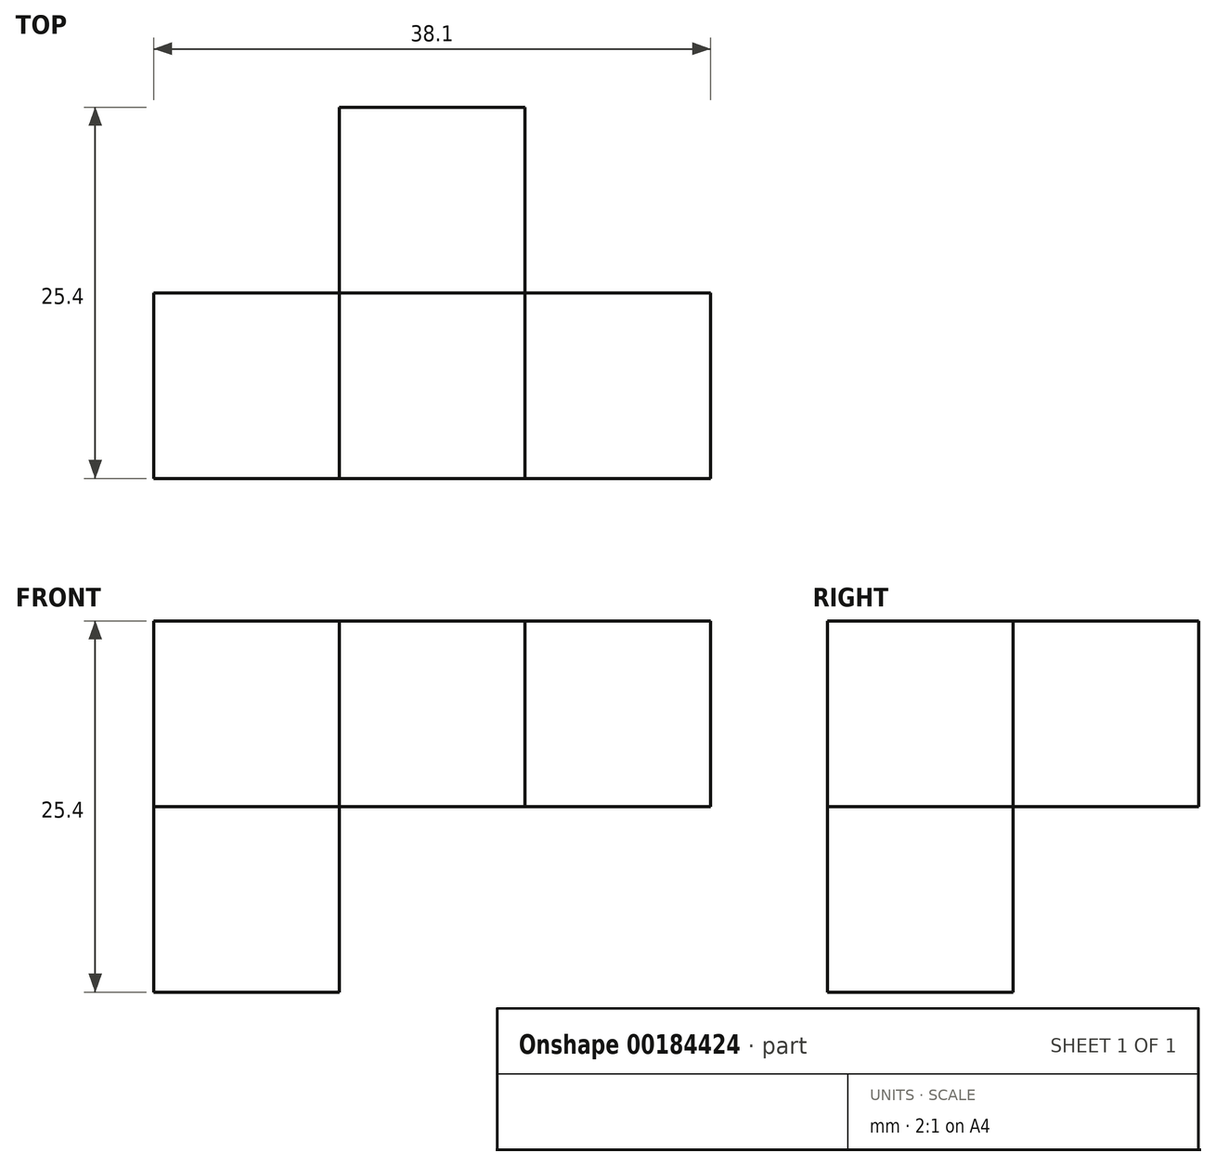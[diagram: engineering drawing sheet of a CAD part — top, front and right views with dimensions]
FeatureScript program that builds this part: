
annotation { "Feature Type Name" : "Feature", "Feature Type Description" : "" }
export const myFeature = defineFeature(function(context is Context, id is Id, definition is map)
    precondition{}
    {
        {
            var Q0;
            Q0=qCreatedBy(makeId("Front.planeOp"),FACE);
            var sketch = newSketch(context, id + "F0", { "sketchPlane" : qUnion([Q0])});
            skLineSegment(sketch, "E0.bottom", {"start": v(53.53, 16.57) * mm, "end": v(66.23, 16.57) * mm});
            skLineSegment(sketch, "E0.top", {"start": v(53.53, 3.87) * mm, "end": v(66.23, 3.87) * mm});
            skLineSegment(sketch, "E0.left", {"start": v(53.53, 16.57) * mm, "end": v(53.53, 3.87) * mm});
            skLineSegment(sketch, "E0.right", {"start": v(66.23, 16.57) * mm, "end": v(66.23, 3.87) * mm});
            skSolve(sketch);
        }
        {
            var Q0;
            Q0 = qSketchRegion(id + "F0", true);
            extrude(context, id + "F1", {"entities" : qUnion([Q0]), "depth" : 12.7 * mm});
        }
        {
            var Q0;
            Q0=makeQuery(id+"F1.opExtrude","SWEPT_EDGE",EDGE,{"disambiguationData":[OSD([sQuery(id+"F0.wireOp",EDGE,"E0.bottom"),sQuery(id+"F0.wireOp",EDGE,"E0.right")])]});
            cPoint(context, id + "F2", {"entities" : qUnion([Q0]), "parameter" : 0.5});
        }
        {
            var Q0;
            Q0=makeQuery(id+"F1.opExtrude","SWEPT_EDGE",EDGE,{"disambiguationData":[OSD([sQuery(id+"F0.wireOp",EDGE,"E0.bottom"),sQuery(id+"F0.wireOp",EDGE,"E0.left")])]});
            cPoint(context, id + "F3", {"entities" : qUnion([Q0]), "parameter" : 0.5});
        }
        {
            var Q0;
            Q0=makeQuery(id+"F1.opExtrude","SWEPT_BODY",BODY,{"disambiguationData":[OSD([sQuery(id+"F0.wireOp",EDGE,"E0.bottom"),sQuery(id+"F0.wireOp",EDGE,"E0.top"),sQuery(id+"F0.wireOp",EDGE,"E0.left"),sQuery(id+"F0.wireOp",EDGE,"E0.right")])]});
            var Q1;
            Q1 = qCreatedBy(id + "F2" ,VERTEX);
            var Q2;
            Q2 = qCreatedBy(id + "F3" ,VERTEX);
            transform(context, id + "F4", {"entities" : qUnion([Q0]), "transformType" : TransformType.TRANSLATION_ENTITY, "oppositeDirectionEntity" : false, "transformLine" : qUnion([Q1, Q2]), "makeCopy" : true});
        }
        {
            var Q0;
            Q0=makeQuery(id+"F4.opPattern","COPY",BODY,{"derivedFrom":makeQuery(id+"F1.opExtrude","SWEPT_BODY",BODY,{"disambiguationData":[OSD([sQuery(id+"F0.wireOp",EDGE,"E0.bottom"),sQuery(id+"F0.wireOp",EDGE,"E0.top"),sQuery(id+"F0.wireOp",EDGE,"E0.left"),sQuery(id+"F0.wireOp",EDGE,"E0.right")])]}),"instanceName":"1"});
            var Q1;
            Q1=makeQuery(id+"F4.opPattern","COPY",VERTEX,{"derivedFrom":makeQuery(id+"F1.opExtrude","CAP_VERTEX",VERTEX,{"disambiguationData":[OSD([sQuery(id+"F0.wireOp",EDGE,"E0.bottom"),sQuery(id+"F0.wireOp",EDGE,"E0.left")])],"isStart":false}),"instanceName":"1"});
            var Q2;
            Q2=makeQuery(id+"F4.opPattern","COPY",VERTEX,{"derivedFrom":makeQuery(id+"F1.opExtrude","CAP_VERTEX",VERTEX,{"disambiguationData":[OSD([sQuery(id+"F0.wireOp",EDGE,"E0.bottom"),sQuery(id+"F0.wireOp",EDGE,"E0.left")])],"isStart":true}),"instanceName":"1"});
            transform(context, id + "F5", {"entities" : qUnion([Q0]), "transformType" : TransformType.TRANSLATION_ENTITY, "oppositeDirectionEntity" : false, "transformLine" : qUnion([Q1, Q2]), "makeCopy" : true});
        }
        {
            var Q0;
            Q0=makeQuery(id+"F1.opExtrude","SWEPT_EDGE",EDGE,{"disambiguationData":[OSD([sQuery(id+"F0.wireOp",EDGE,"E0.bottom"),sQuery(id+"F0.wireOp",EDGE,"E0.left")])]});
            cPoint(context, id + "F6", {"entities" : qUnion([Q0]), "parameter" : 0.5});
        }
        {
            var Q0;
            Q0=makeQuery(id+"F4.opPattern","COPY",EDGE,{"derivedFrom":makeQuery(id+"F1.opExtrude","SWEPT_EDGE",EDGE,{"disambiguationData":[OSD([sQuery(id+"F0.wireOp",EDGE,"E0.bottom"),sQuery(id+"F0.wireOp",EDGE,"E0.left")])]}),"instanceName":"1"});
            cPoint(context, id + "F7", {"entities" : qUnion([Q0]), "parameter" : 0.5});
        }
        {
            var Q0;
            Q0=makeQuery(id+"F4.opPattern","COPY",BODY,{"derivedFrom":makeQuery(id+"F1.opExtrude","SWEPT_BODY",BODY,{"disambiguationData":[OSD([sQuery(id+"F0.wireOp",EDGE,"E0.bottom"),sQuery(id+"F0.wireOp",EDGE,"E0.top"),sQuery(id+"F0.wireOp",EDGE,"E0.left"),sQuery(id+"F0.wireOp",EDGE,"E0.right")])]}),"instanceName":"1"});
            var Q1;
            Q1 = qCreatedBy(id + "F6" ,VERTEX);
            var Q2;
            Q2 = qCreatedBy(id + "F7" ,VERTEX);
            transform(context, id + "F8", {"entities" : qUnion([Q0]), "transformType" : TransformType.TRANSLATION_ENTITY, "oppositeDirectionEntity" : false, "transformLine" : qUnion([Q1, Q2]), "makeCopy" : true});
        }
        {
            var Q0;
            Q0=makeQuery(id+"F8.opPattern","COPY",BODY,{"derivedFrom":makeQuery(id+"F4.opPattern","COPY",BODY,{"derivedFrom":makeQuery(id+"F1.opExtrude","SWEPT_BODY",BODY,{"disambiguationData":[OSD([sQuery(id+"F0.wireOp",EDGE,"E0.bottom"),sQuery(id+"F0.wireOp",EDGE,"E0.top"),sQuery(id+"F0.wireOp",EDGE,"E0.left"),sQuery(id+"F0.wireOp",EDGE,"E0.right")])]}),"instanceName":"1"}),"instanceName":"1"});
            transform(context, id + "F9", {"entities" : qUnion([Q0]), "transformType" : TransformType.TRANSLATION_3D, "dx" : 0 * mm, "dy" : 0 * mm, "dz" : -12.7 * mm, "makeCopy" : true});
        }
    });
